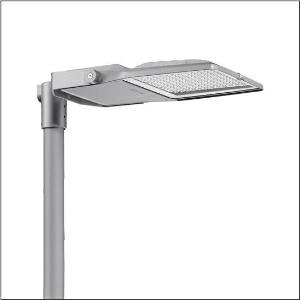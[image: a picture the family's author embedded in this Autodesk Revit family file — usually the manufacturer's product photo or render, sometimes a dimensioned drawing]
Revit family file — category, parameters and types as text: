
# Revit family: floodlight_fl_21_iq_midi___pl61_5xa7782e4c3a_83e0
name_source: partatom
category: Lighting Fixtures
units: mm (PartAtom-declared; Revit-internal decimal feet)

## family parameters
Cut with Voids When Loaded = No
Host = Face
Light Source = No
Part Type = Normal
Room Calculation Point = No
Round Connector Dimension = Use Diameter
Shared = No

## types (1)
- --- (1 x LED, 27490 lm, 208.1 W, 4000K)
    Apparent Load = 208 VA
    CIE Flux Codes = 33 65 98 100 100
    Color Rendering = 70
    Color Temperature = 4000K
    Default Elevation = 1800 mm
    Description = Floodlight FL 21 iQ midi, floodlight, primary light control with lens, of PMMA, primary optical cover: protective disc, of toughened safety glass, transparent, light distribution: PL61, light emission: direct distribution, installation type: surface-mounted, LED, High Power LED, rated luminous flux: 27.490lm, luminous efficacy: 132lm/W, light colour: 740, colour temperature: 4000K, control gear: ECG iQ, control: optimised constant luminous flux control (CLO 2.0), Desk-Remote (wireless, voltage-free reading and setting of iQ features in the workshop via application-optimized NFC function/RFID function), Smart-Wire, Night-Set, Temp-Guard, Auto-Match, Street-Remote, with terminal, 6-pole, mains connection: 220..240V, AC, 50/60Hz, start of lifetime: 208W, end of service life: 227W, reduction: 90W, luminaire housing, of diecast aluminium, powder-coated, Siteco® metallic grey (DB 702S), corrosivity category C5 mid according to DIN EN ISO 12944, sealing non-destructively replaceable, please order mast flange separately, mast bracket, of steel, galvanised, powder-coated, Siteco® metallic grey (DB 702S), protection rating (complete): IP66, insulation class (complete): insulation class II (safety insulation), certification: CE, protection symbol: D, impact resistance: IK08, permissible operating ambient temperature: -40..+40°C, permissible operating ambient temperature for outdoor applications: -40..+50°C, standard: DIN EN 12944, LABS conformity tested according to VDMA 24364:2018-05, packaging unit: 1 piece

Light Distribution: PL61
    Height = 76 mm
    Lamp = 1 x LED
    Lamp Light Flux = 27490 lm
    Lamp Power = 208.1 W
    Lamp count = 1
    Length = 657 mm
    Luminous efficacy = 132 lm/W
    Manufacturer = Siteco
    ModVariant = No
    Model = 5XA7782E4C3A
    Number of Poles = 1
    OnlyDefault = Yes
    Power Factor = 1
    Product Name = Floodlight FL 21 iQ midi | PL61
    Product group = floodlight | pylon annexe
    ProductGroupID = 6200
    Protection Class = Protection class II
    Protection Degree = IP 66
    RLX_Detail_Level = 1
    RLX_Emergency_Light_Flux = 0 lm
    RLX_Emergency_Type = 0
    RLX_Emergency_Type_DB = No
    RlxData = <blob elided: 153821 chars, md5=4651b569>
    Socket = socket
    Standby Power = 0 W
    System Light Flux = 27490 lm
    System Power = 208 W
    Type Comments = factory setting: luminous flux: 100 % | dim-lin: 254 | 710 mA
    Type Image = l_1007123.jpg
    URL = http://relux.com
    VarID = @adj_038761
    Voltage = 0 V
    Weight = 0.00 kg
    Width = 442 mm

## geometry (parser evidence)
native form markers: Blend x4, Sweep x12
no freeform markers — native parametric forms only
